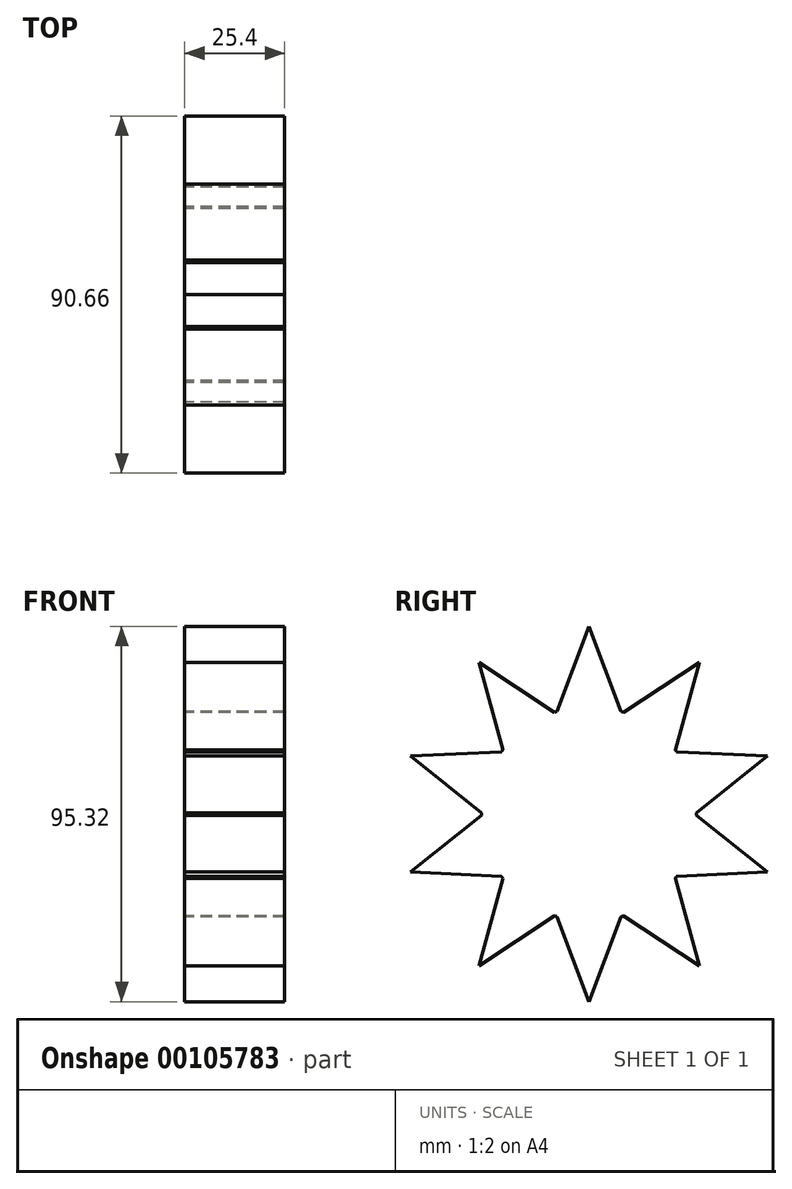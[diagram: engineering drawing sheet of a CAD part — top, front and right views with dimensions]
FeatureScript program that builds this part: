
annotation { "Feature Type Name" : "Feature", "Feature Type Description" : "" }
export const myFeature = defineFeature(function(context is Context, id is Id, definition is map)
    precondition{}
    {
        {
            var Q0;
            Q0=qCreatedBy(makeId("Right.planeOp"),FACE);
            var sketch = newSketch(context, id + "F0", { "sketchPlane" : qUnion([Q0])});
            skCircle(sketch, "E0", {"center": v(0, 0) * mm, "radius": 27.32 * mm});
            skLineSegment(sketch, "E1", {"start": v(-8.12, 26.08) * mm, "end": v(0, 47.66) * mm});
            skLineSegment(sketch, "E2.MirrorCS", {"start": v(8.12, 26.08) * mm, "end": v(0, 47.66) * mm});
            skLineSegment(sketch, "E3.1.0", {"start": v(-8.76, 25.87) * mm, "end": v(-28.02, 38.56) * mm});
            skLineSegment(sketch, "E3.1.1", {"start": v(-21.9, 16.33) * mm, "end": v(-28.02, 38.56) * mm});
            skLineSegment(sketch, "E3.2.0", {"start": v(-22.3, 15.78) * mm, "end": v(-45.33, 14.73) * mm});
            skLineSegment(sketch, "E3.2.1", {"start": v(-27.31, 0.34) * mm, "end": v(-45.33, 14.73) * mm});
            skLineSegment(sketch, "E3.3.0", {"start": v(-27.31, -0.34) * mm, "end": v(-45.33, -14.73) * mm});
            skLineSegment(sketch, "E3.3.1", {"start": v(-22.3, -15.78) * mm, "end": v(-45.33, -14.73) * mm});
            skLineSegment(sketch, "E3.4.0", {"start": v(-21.9, -16.33) * mm, "end": v(-28.02, -38.56) * mm});
            skLineSegment(sketch, "E3.4.1", {"start": v(-8.76, -25.87) * mm, "end": v(-28.02, -38.56) * mm});
            skLineSegment(sketch, "E3.5.0", {"start": v(-8.12, -26.08) * mm, "end": v(0, -47.66) * mm});
            skLineSegment(sketch, "E3.5.1", {"start": v(8.12, -26.08) * mm, "end": v(0, -47.66) * mm});
            skLineSegment(sketch, "E3.6.0", {"start": v(8.76, -25.87) * mm, "end": v(28.02, -38.56) * mm});
            skLineSegment(sketch, "E3.6.1", {"start": v(21.9, -16.33) * mm, "end": v(28.02, -38.56) * mm});
            skLineSegment(sketch, "E3.7.0", {"start": v(22.3, -15.78) * mm, "end": v(45.33, -14.73) * mm});
            skLineSegment(sketch, "E3.7.1", {"start": v(27.31, -0.34) * mm, "end": v(45.33, -14.73) * mm});
            skLineSegment(sketch, "E3.8.0", {"start": v(27.31, 0.34) * mm, "end": v(45.33, 14.73) * mm});
            skLineSegment(sketch, "E3.8.1", {"start": v(22.3, 15.78) * mm, "end": v(45.33, 14.73) * mm});
            skLineSegment(sketch, "E3.9.0", {"start": v(21.9, 16.33) * mm, "end": v(28.02, 38.56) * mm});
            skLineSegment(sketch, "E3.9.1", {"start": v(8.76, 25.87) * mm, "end": v(28.02, 38.56) * mm});
            skSolve(sketch);
        }
        {
            var Q0;
            Q0 = qSketchRegion(id + "F0", true);
            extrude(context, id + "F1", {"entities" : qUnion([Q0]), "depth" : 25.4 * mm});
        }
    });
